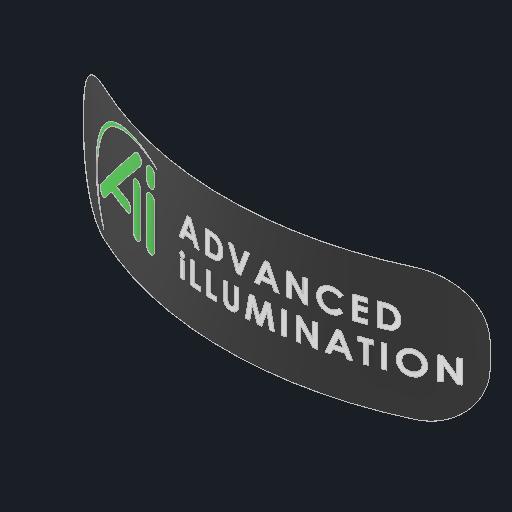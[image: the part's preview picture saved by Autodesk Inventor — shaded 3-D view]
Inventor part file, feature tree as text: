
AUTODESK INVENTOR PART (.ipt)
format: ipt  version: 2025 (Build 290162000, 162)  size: 834,560 bytes
history: native  units: in
note: dims shown in document units (in); Inventor stores cm internally (conversion verified against a paired STEP export)
features: fillet x1
ambient origin geometry x8: Origin, YZ Plane, XZ Plane, XY Plane, X Axis, Y Axis, Z Axis, Center Point
bodies: Solid1 (feature_tree)
feature tree (1):
  fillet  "Fillet1"  [1 undecoded]
note: 1 required parameter value undecoded (feature->parameter linkage not recoverable at this tier; creation-order binding heuristic only, values carry confidence <= 0.55)
